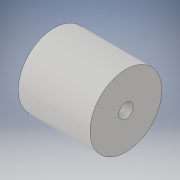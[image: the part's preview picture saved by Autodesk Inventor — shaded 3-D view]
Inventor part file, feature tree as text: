
AUTODESK INVENTOR PART (.ipt)
format: ipt  version: 2019 (Build 230136000, 136)  size: 104,448 bytes
history: native  units: mm
features: extrude x3, sketch x3, other x1
ambient origin geometry x8: Origin, YZ Plane, XZ Plane, XY Plane, X Axis, Y Axis, Z Axis, Center Point
bodies: Body1 (feature_tree)
feature tree (7):
  other  "Твердое тело1"
  extrude  "Выдавливание1"  Depth=10.0mm
  extrude  "Выдавливание2"  Depth=10.0mm TaperAngle=0.0deg
  extrude  "Выдавливание3"  Depth=2.15mm
  sketch  "Эскиз1"
  sketch  "Эскиз2"
  sketch  "Эскиз4"
